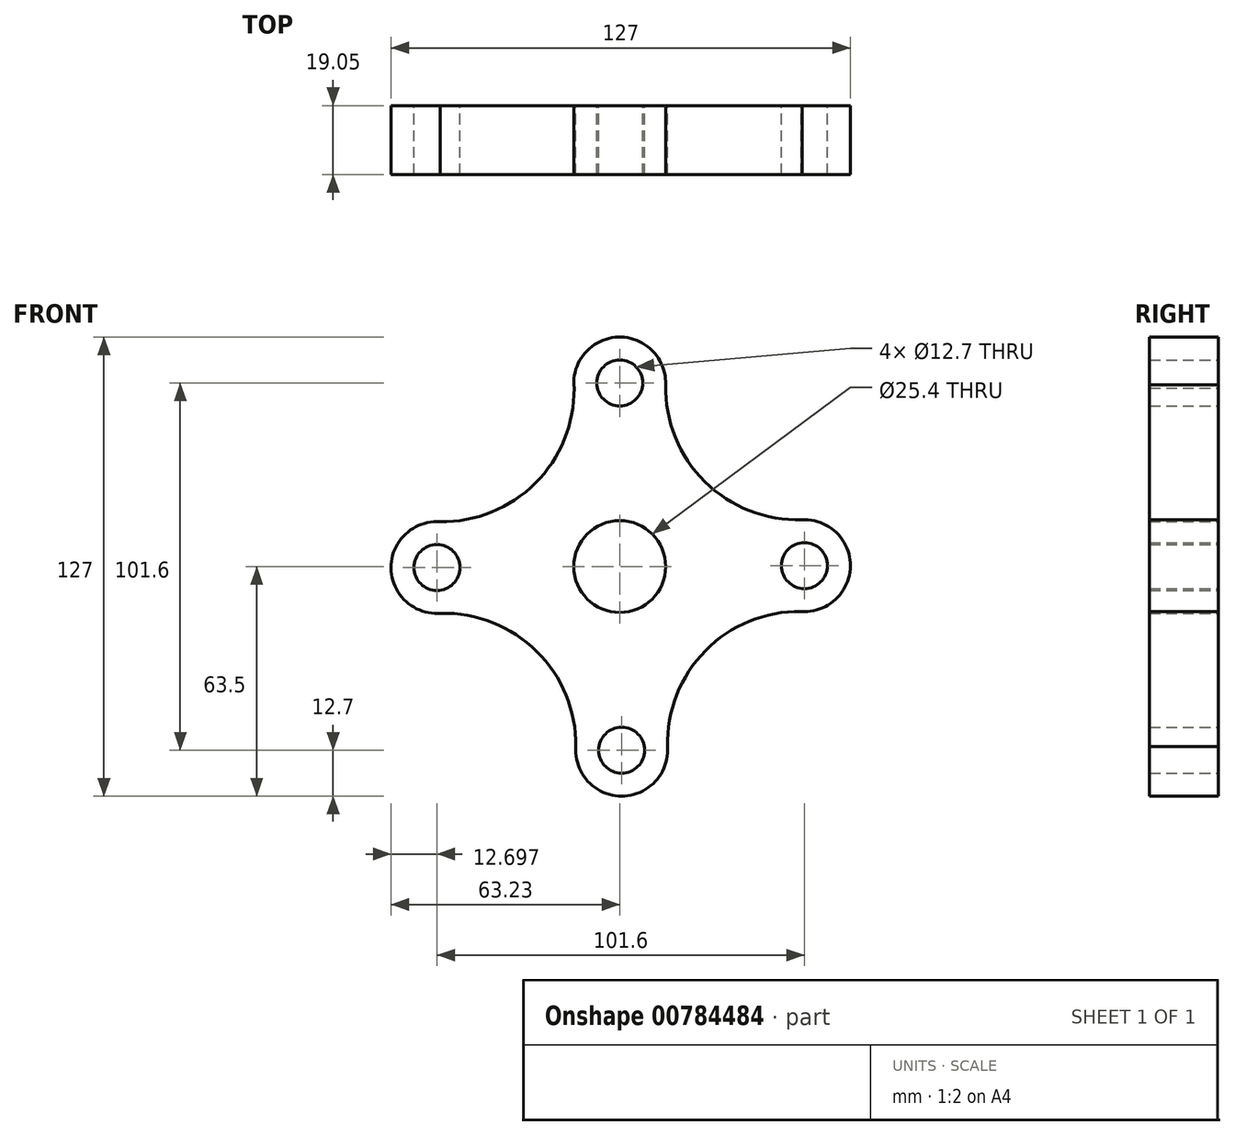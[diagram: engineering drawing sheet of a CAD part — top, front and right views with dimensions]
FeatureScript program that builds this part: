
annotation { "Feature Type Name" : "Feature", "Feature Type Description" : "" }
export const myFeature = defineFeature(function(context is Context, id is Id, definition is map)
    precondition{}
    {
        {
            var Q0;
            Q0=qCreatedBy(makeId("Front.planeOp"),FACE);
            var sketch = newSketch(context, id + "F0", { "sketchPlane" : qUnion([Q0])});
            skCircle(sketch, "E0", {"center": v(0, 0) * mm, "radius": 12.7 * mm});
            skCircle(sketch, "E1", {"center": v(0, 50.8) * mm, "radius": 6.35 * mm});
            skCircle(sketch, "E2.1.0", {"center": v(-50.53, -0.27) * mm, "radius": 6.35 * mm});
            skCircle(sketch, "E2.2.0", {"center": v(0.53, -50.8) * mm, "radius": 6.35 * mm});
            skCircle(sketch, "E2.3.0", {"center": v(51.07, 0.27) * mm, "radius": 6.35 * mm});
            skPoint(sketch, "E2.center", {"position": v(0.27, 0) * mm});
            skArc(sketch, "E3", {"start": v(12.69, 50.23) * mm, "mid": v(-0.43, 63.5) * mm, "end": v(-12.62, 49.37) * mm});
            skArc(sketch, "E4", {"start": v(-49.65, 12.4) * mm, "mid": v(-63.23, -0.4) * mm, "end": v(-49.4, -12.92) * mm});
            skArc(sketch, "E5", {"start": v(-12.13, -49.8) * mm, "mid": v(0.5, -63.5) * mm, "end": v(13.2, -49.86) * mm});
            skArc(sketch, "E6", {"start": v(50.16, -12.4) * mm, "mid": v(63.77, 0.15) * mm, "end": v(50.39, 12.95) * mm});
            skArc(sketch, "E7", {"start": v(12.7, 50.67) * mm, "mid": v(23.36, 23.64) * mm, "end": v(50.39, 12.95) * mm});
            skArc(sketch, "E8", {"start": v(-50.7, 12.43) * mm, "mid": v(-23.04, 23.38) * mm, "end": v(-12.7, 51.26) * mm});
            skArc(sketch, "E9", {"start": v(-12.16, -51.09) * mm, "mid": v(-22.96, -23.47) * mm, "end": v(-50.7, -12.97) * mm});
            skArc(sketch, "E10", {"start": v(51.28, -12.43) * mm, "mid": v(23.78, -23.2) * mm, "end": v(13.23, -50.77) * mm});
            skSolve(sketch);
        }
        {
            var Q0;
            Q0 = qSketchRegion(id + "F0", true);
            extrude(context, id + "F1", {"entities" : qUnion([Q0]), "depth" : 19.05 * mm, "offsetDistance" : 25.4 * mm});
        }
    });
